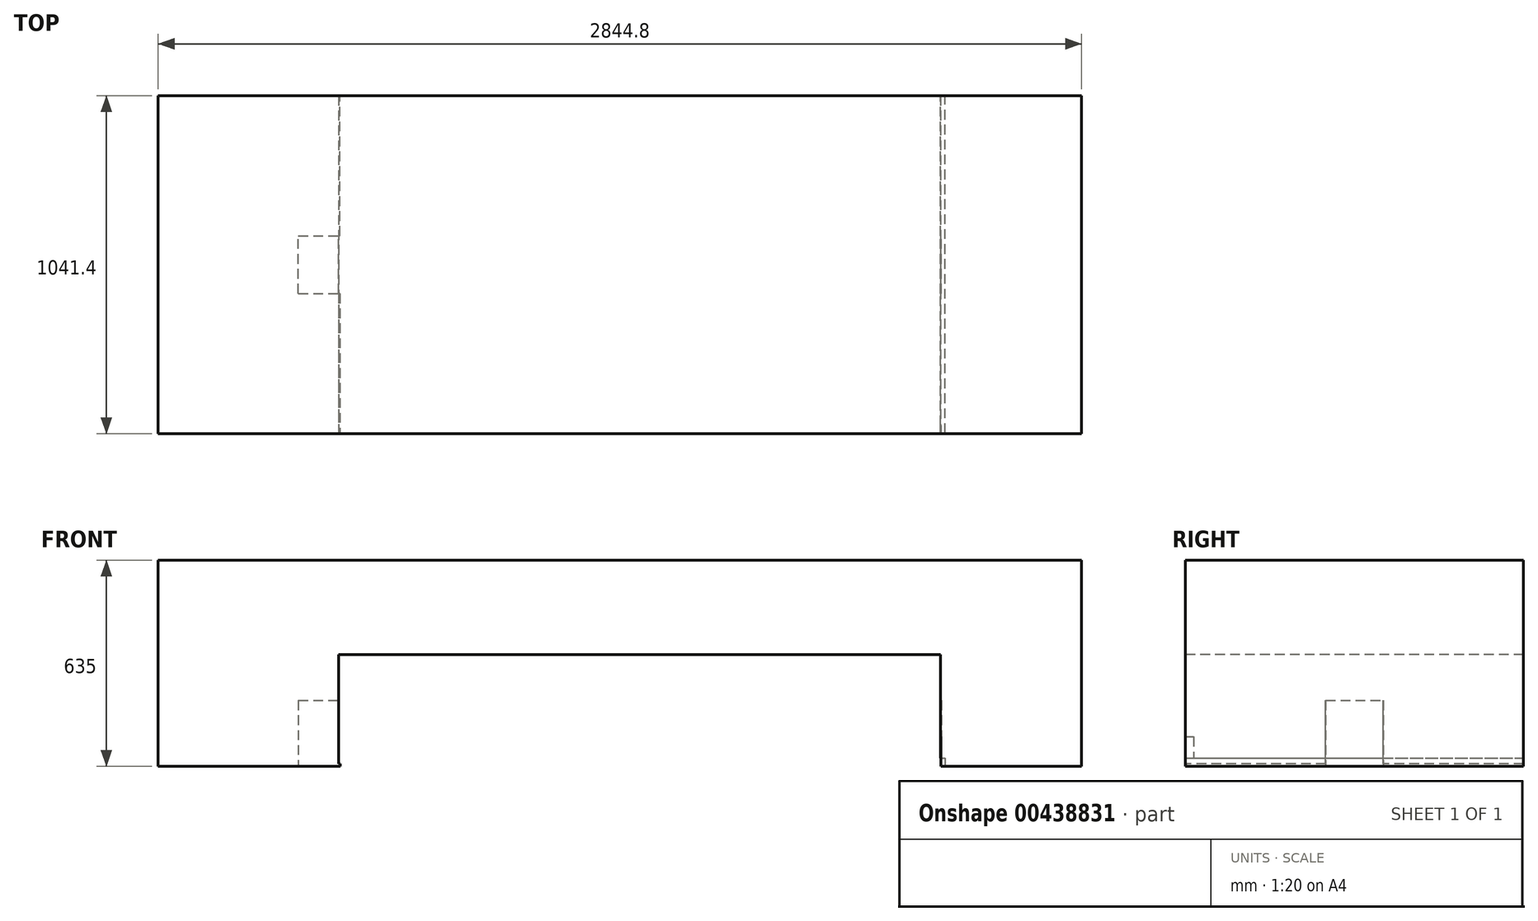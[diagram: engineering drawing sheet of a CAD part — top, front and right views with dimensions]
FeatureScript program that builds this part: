
annotation { "Feature Type Name" : "Feature", "Feature Type Description" : "" }
export const myFeature = defineFeature(function(context is Context, id is Id, definition is map)
    precondition{}
    {
        {
            var Q0;
            Q0=qCreatedBy(makeId("Front.planeOp"),FACE);
            var sketch = newSketch(context, id + "F0", { "sketchPlane" : qUnion([Q0])});
            skLineSegment(sketch, "E0.bottom", {"start": v(-2789.46, 595.4) * mm, "end": v(55.34, 595.4) * mm});
            skLineSegment(sketch, "E0.top", {"start": v(-2789.46, -39.6) * mm, "end": v(55.34, -39.6) * mm});
            skLineSegment(sketch, "E0.left", {"start": v(-2789.46, 595.4) * mm, "end": v(-2789.46, -39.6) * mm});
            skLineSegment(sketch, "E0.right", {"start": v(55.34, 595.4) * mm, "end": v(55.34, -39.6) * mm});
            skSolve(sketch);
        }
        {
            var Q0;
            Q0=makeQuery(id+"F0.imprint","IMPRINT",FACE,{"disambiguationData":[TD([[makeQuery(id+"F0.imprint","IMPRINT",EDGE,{"derivedFrom":sQuery(id+"F0.wireOp",EDGE,"E0.bottom")}),-1.0]])]});
            extrude(context, id + "F1", {"entities" : qUnion([Q0]), "depth" : 1041.4 * mm});
        }
        {
            var Q0;
            Q0=makeQuery(id+"F1.opExtrude","SWEPT_FACE",FACE,{"disambiguationData":[OSD([sQuery(id+"F0.wireOp",EDGE,"E0.top")])]});
            shell(context, id + "F2", {"entities" : qUnion([Q0]), "thickness" : 431.8 * mm});
        }
        {
            var Q0;
            Q0=makeQuery(id+"F1.opExtrude","CAP_FACE",FACE,{"disambiguationData":[OSD([sQuery(id+"F0.wireOp",EDGE,"E0.bottom"),sQuery(id+"F0.wireOp",EDGE,"E0.top"),sQuery(id+"F0.wireOp",EDGE,"E0.left"),sQuery(id+"F0.wireOp",EDGE,"E0.right")])],"isStart":false});
            var sketch = newSketch(context, id + "F3", { "sketchPlane" : qUnion([Q0])});
            skLineSegment(sketch, "E1.bottom", {"start": v(55.17, -35.32) * mm, "end": v(-636.47, -35.32) * mm});
            skLineSegment(sketch, "E1.left", {"start": v(55.17, -35.32) * mm, "end": v(55.17, 150.32) * mm});
            skLineSegment(sketch, "E2.bottom", {"start": v(52.18, -32.33) * mm, "end": v(-2791.35, -32.33) * mm});
            skLineSegment(sketch, "E2.top", {"start": v(52.18, 596.94) * mm, "end": v(-2791.35, 596.94) * mm});
            skLineSegment(sketch, "E2.left", {"start": v(52.18, -32.33) * mm, "end": v(52.18, 596.94) * mm});
            skLineSegment(sketch, "E2.right", {"start": v(-2791.35, -32.33) * mm, "end": v(-2791.35, 596.94) * mm});
            skArc(sketch, "E3", {"start": v(-2787.11, -29.74) * mm, "mid": v(-2787.12, -31.03) * mm, "end": v(-2787.13, -32.33) * mm});
            skPoint(sketch, "E3.first.point", {"position": v(-2787.11, -29.74) * mm});
            skPoint(sketch, "E3.second.point", {"position": v(54.13, -42.45) * mm});
            skPoint(sketch, "E3.third.point", {"position": v(-311.67, -991) * mm});
            skLineSegment(sketch, "E4.top", {"start": v(-380.22, 305.07) * mm, "end": v(-2234.42, 305.07) * mm});
            skLineSegment(sketch, "E4.left", {"start": v(-380.22, -35.32) * mm, "end": v(-380.22, 305.07) * mm});
            skLineSegment(sketch, "E4.right", {"start": v(-2234.42, -32.33) * mm, "end": v(-2234.42, 305.07) * mm});
            skPoint(sketch, "E4.middle", {"position": v(-1307.32, -43.87) * mm});
            skArc(sketch, "E5.trimOffspring", {"start": v(54.13, -42.45) * mm, "mid": v(53.68, -3.69) * mm, "end": v(52.18, 35.04) * mm});
            skPoint(sketch, "E4.bottom.end.orphan", {"position": v(-2234.42, -392.82) * mm});
            skPoint(sketch, "E6.orphan", {"position": v(-380.22, -392.82) * mm});
            skSolve(sketch);
        }
        {
            var Q0;
            {var subQ4=sQuery(id+"F3.wireOp",EDGE,"E4.top");Q0=makeQuery(id+"F3.imprint","IMPRINT",FACE,{"disambiguationData":[TD([[makeQuery(id+"F3.imprint","IMPRINT",EDGE,{"derivedFrom":subQ4}),1.0]])]});}
            extrude(context, id + "F4", {"entities" : qUnion([Q0]), "operationType" : NewBodyOperationType.REMOVE, "oppositeDirection" : true, "depth" : 1041.4 * mm});
        }
        {
            var Q0;
            Q0=makeQuery(id+"F1.opExtrude","SWEPT_FACE",FACE,{"disambiguationData":[OSD([sQuery(id+"F0.wireOp",EDGE,"E0.top")])]});
            var sketch = newSketch(context, id + "F5", { "sketchPlane" : qUnion([Q0])});
            skLineSegment(sketch, "E7.bottom", {"start": v(-2230.4, 1039.34) * mm, "end": v(-365.97, 1039.34) * mm});
            skLineSegment(sketch, "E7.top", {"start": v(-2230.4, -5.03) * mm, "end": v(-365.97, -5.03) * mm});
            skLineSegment(sketch, "E7.left", {"start": v(-2230.4, 1039.34) * mm, "end": v(-2230.4, -5.03) * mm});
            skLineSegment(sketch, "E7.right", {"start": v(-365.97, 1039.34) * mm, "end": v(-365.97, -5.03) * mm});
            skSolve(sketch);
        }
        {
            var Q0;
            Q0 = qSketchRegion(id + "F5", true);
            extrude(context, id + "F6", {"entities" : qUnion([Q0]), "operationType" : NewBodyOperationType.REMOVE, "oppositeDirection" : true, "depth" : 25.4 * mm});
        }
        {
            var Q0;
            Q0=makeQuery(id+"F1.opExtrude","CAP_FACE",FACE,{"disambiguationData":[OSD([sQuery(id+"F0.wireOp",EDGE,"E0.bottom"),sQuery(id+"F0.wireOp",EDGE,"E0.top"),sQuery(id+"F0.wireOp",EDGE,"E0.left"),sQuery(id+"F0.wireOp",EDGE,"E0.right")])],"isStart":false});
            var sketch = newSketch(context, id + "F7", { "sketchPlane" : qUnion([Q0])});
            skLineSegment(sketch, "E8.bottom", {"start": v(-2229.35, 51.5) * mm, "end": v(-378.98, 51.5) * mm});
            skLineSegment(sketch, "E8.top", {"start": v(-2229.35, -122.15) * mm, "end": v(-378.98, -122.15) * mm});
            skLineSegment(sketch, "E8.left", {"start": v(-2229.35, 51.5) * mm, "end": v(-2229.35, -122.15) * mm});
            skLineSegment(sketch, "E8.right", {"start": v(-378.98, 51.5) * mm, "end": v(-378.98, -122.15) * mm});
            skSolve(sketch);
        }
        {
            var Q0;
            Q0 = qSketchRegion(id + "F7", true);
            extrude(context, id + "F8", {"entities" : qUnion([Q0]), "operationType" : NewBodyOperationType.REMOVE, "oppositeDirection" : true, "depth" : 25.4 * mm});
        }
    });
